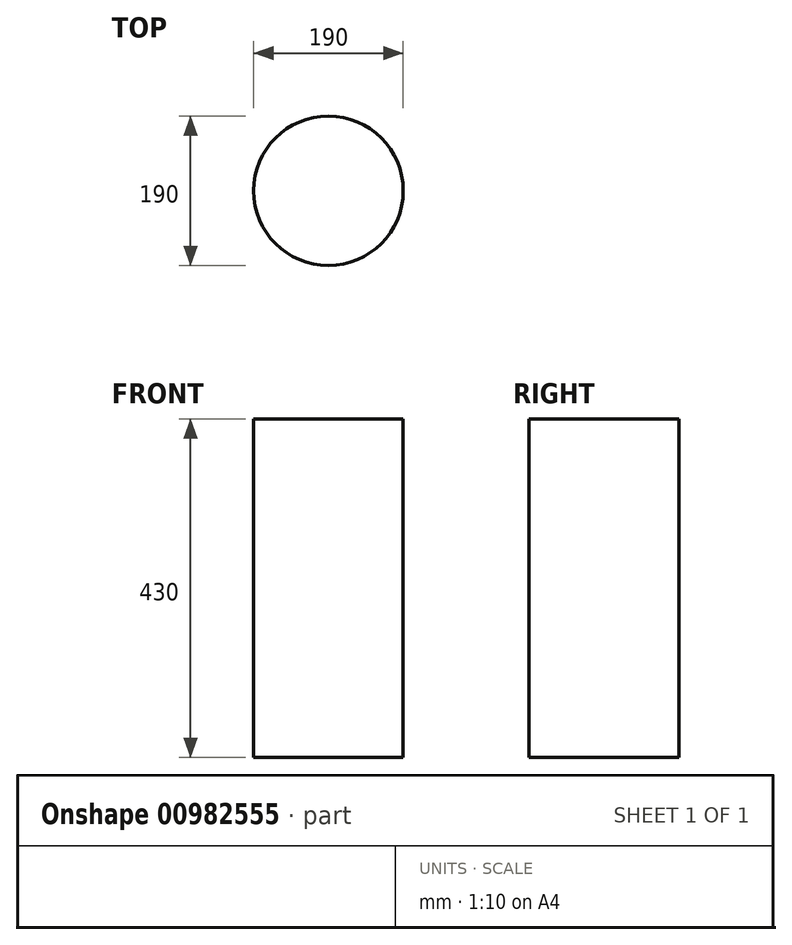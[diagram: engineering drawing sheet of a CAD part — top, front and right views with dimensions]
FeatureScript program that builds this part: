
annotation { "Feature Type Name" : "Feature", "Feature Type Description" : "" }
export const myFeature = defineFeature(function(context is Context, id is Id, definition is map)
    precondition{}
    {
        {
            var Q0;
            Q0=qCreatedBy(makeId("Top.planeOp"),FACE);
            var sketch = newSketch(context, id + "F0", { "sketchPlane" : qUnion([Q0])});
            skCircle(sketch, "E0", {"center": v(0, 0) * mm, "radius": 95 * mm});
            skSolve(sketch);
        }
        {
            var Q0;
            Q0=qCreatedBy(makeId("Front.planeOp"),FACE);
            var sketch = newSketch(context, id + "F1", { "sketchPlane" : qUnion([Q0])});
            skLineSegment(sketch, "E1", {"start": v(0, 0) * mm, "end": v(0, 430) * mm});
            skSolve(sketch);
        }
        {
            var Q0;
            Q0=makeQuery(id+"F0.imprint","IMPRINT",FACE,{"disambiguationData":[TD([[makeQuery(id+"F0.imprint","IMPRINT",EDGE,{"derivedFrom":sQuery(id+"F0.wireOp",EDGE,"E0")}),1.0]])]});
            var Q1;
            Q1=sQuery(id+"F1.wireOp",EDGE,"E1");
            sweep(context, id + "F2", {"profiles" : qUnion([Q0]), "path" : qUnion([Q1])});
        }
    });
